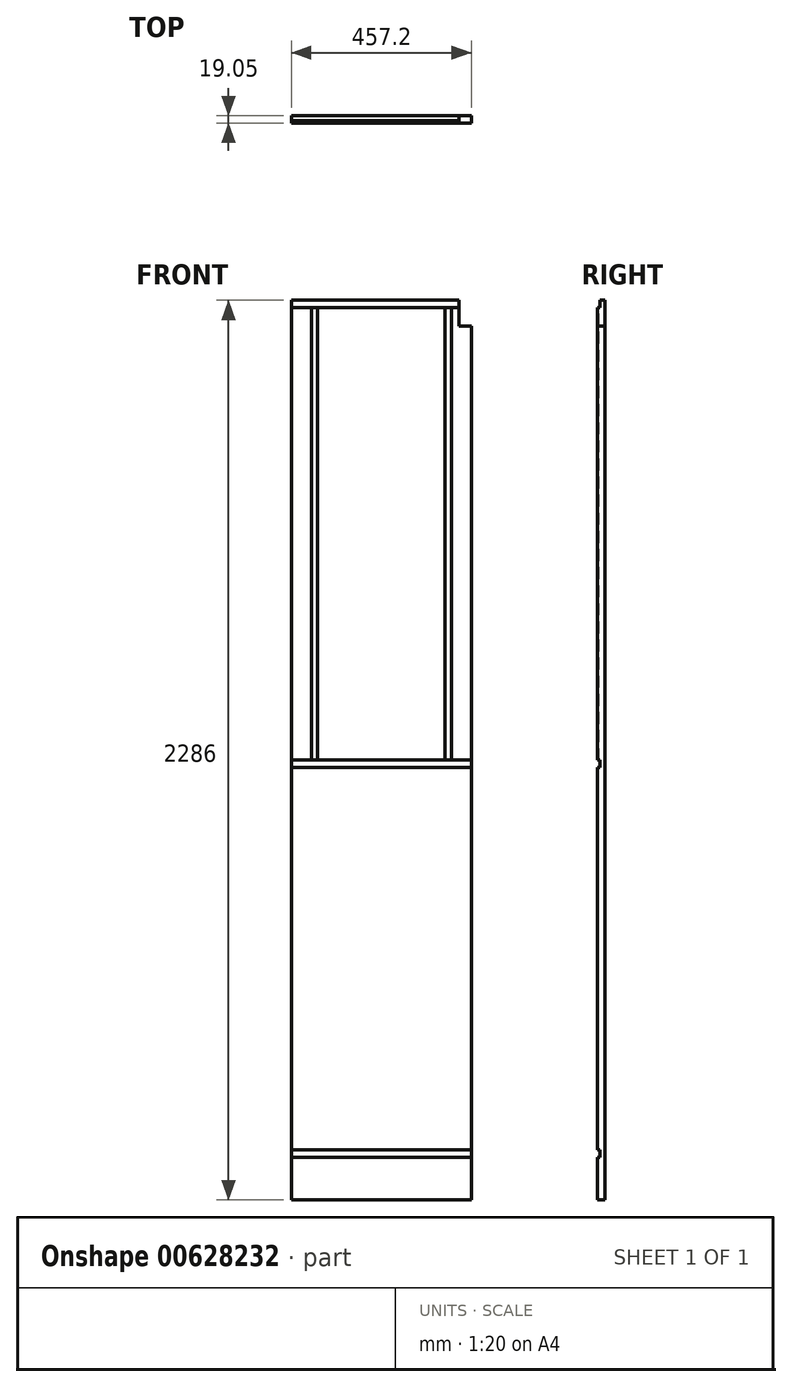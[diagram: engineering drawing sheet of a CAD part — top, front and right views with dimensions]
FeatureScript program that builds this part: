
annotation { "Feature Type Name" : "Feature", "Feature Type Description" : "" }
export const myFeature = defineFeature(function(context is Context, id is Id, definition is map)
    precondition{}
    {
        {
            var Q0;
            Q0=qCreatedBy(makeId("Front.planeOp"),FACE);
            var sketch = newSketch(context, id + "F0", { "sketchPlane" : qUnion([Q0])});
            skLineSegment(sketch, "E0.bottom", {"start": v(0, 0) * mm, "end": v(457.2, 0) * mm});
            skLineSegment(sketch, "E0.top", {"start": v(0, 2286) * mm, "end": v(457.2, 2286) * mm});
            skLineSegment(sketch, "E0.left", {"start": v(0, 0) * mm, "end": v(0, 2286) * mm});
            skLineSegment(sketch, "E0.right", {"start": v(457.2, 0) * mm, "end": v(457.2, 2286) * mm});
            skSolve(sketch);
        }
        {
            var Q0;
            Q0=qSketchRegion(id+"F0",true);
            extrude(context, id + "F1", {"entities" : qUnion([Q0]), "depth" : 19.05 * mm, "offsetDistance" : 25.4 * mm});
        }
        {
            var Q0;
            Q0=makeQuery(id+"F1.opExtrude","CAP_FACE",FACE,{"disambiguationData":[OSD([sQuery(id+"F0.wireOp",EDGE,"E0.bottom"),sQuery(id+"F0.wireOp",EDGE,"E0.top"),sQuery(id+"F0.wireOp",EDGE,"E0.left"),sQuery(id+"F0.wireOp",EDGE,"E0.right")])],"isStart":false});
            var sketch = newSketch(context, id + "F2", { "sketchPlane" : qUnion([Q0])});
            skLineSegment(sketch, "E1.bottom", {"start": v(457.2, 2286) * mm, "end": v(425.2, 2286) * mm});
            skLineSegment(sketch, "E1.top", {"start": v(457.2, 2219.96) * mm, "end": v(425.2, 2219.96) * mm});
            skLineSegment(sketch, "E1.left", {"start": v(457.2, 2286) * mm, "end": v(457.2, 2219.96) * mm});
            skLineSegment(sketch, "E1.right", {"start": v(425.2, 2286) * mm, "end": v(425.2, 2219.96) * mm});
            skSolve(sketch);
        }
        {
            var Q0;
            Q0=makeQuery(id+"F2.imprint","IMPRINT",FACE,{"disambiguationData":[TD([[makeQuery(id+"F2.imprint","IMPRINT",EDGE,{"derivedFrom":sQuery(id+"F2.wireOp",EDGE,"E1.bottom")}),-1.0]])]});
            extrude(context, id + "F3", {"entities" : qUnion([Q0]), "operationType" : NewBodyOperationType.REMOVE, "endBound" : BoundingType.THROUGH_ALL, "oppositeDirection" : true, "depth" : 25.4 * mm, "offsetDistance" : 25.4 * mm});
        }
        {
            var Q0;
            Q0=makeQuery(id+"F1.opExtrude","CAP_FACE",FACE,{"disambiguationData":[OSD([sQuery(id+"F0.wireOp",EDGE,"E0.bottom"),sQuery(id+"F0.wireOp",EDGE,"E0.top"),sQuery(id+"F0.wireOp",EDGE,"E0.left"),sQuery(id+"F0.wireOp",EDGE,"E0.right")])],"isStart":false});
            var sketch = newSketch(context, id + "F4", { "sketchPlane" : qUnion([Q0])});
            skLineSegment(sketch, "E2.bottom", {"start": v(-11.67, 127) * mm, "end": v(519.07, 127) * mm});
            skLineSegment(sketch, "E2.top", {"start": v(-11.67, 107.7) * mm, "end": v(519.07, 107.7) * mm});
            skLineSegment(sketch, "E2.left", {"start": v(-11.67, 127) * mm, "end": v(-11.67, 107.7) * mm});
            skLineSegment(sketch, "E2.right", {"start": v(519.07, 127) * mm, "end": v(519.07, 107.7) * mm});
            skLineSegment(sketch, "E3.bottom", {"start": v(-24.94, 1117.6) * mm, "end": v(528.35, 1117.6) * mm});
            skLineSegment(sketch, "E3.top", {"start": v(-24.94, 1098.3) * mm, "end": v(528.35, 1098.3) * mm});
            skLineSegment(sketch, "E3.left", {"start": v(-24.94, 1117.6) * mm, "end": v(-24.94, 1098.3) * mm});
            skLineSegment(sketch, "E3.right", {"start": v(528.35, 1117.6) * mm, "end": v(528.35, 1098.3) * mm});
            skLineSegment(sketch, "E4.bottom", {"start": v(-16.64, 2295.24) * mm, "end": v(531.9, 2295.24) * mm});
            skLineSegment(sketch, "E4.top", {"start": v(-16.64, 2266.7) * mm, "end": v(531.9, 2266.7) * mm});
            skLineSegment(sketch, "E4.left", {"start": v(-16.64, 2295.24) * mm, "end": v(-16.64, 2266.7) * mm});
            skLineSegment(sketch, "E4.right", {"start": v(531.9, 2295.24) * mm, "end": v(531.9, 2266.7) * mm});
            skSolve(sketch);
        }
        {
            var Q0;
            Q0=qSketchRegion(id+"F4",true);
            extrude(context, id + "F5", {"entities" : qUnion([Q0]), "operationType" : NewBodyOperationType.REMOVE, "oppositeDirection" : true, "depth" : 6.35 * mm, "offsetDistance" : 25.4 * mm});
        }
        {
            var Q0;
            {var subQ0=sQuery(id+"F0.wireOp",EDGE,"E0.left");var subQ1=sQuery(id+"F0.wireOp",EDGE,"E0.right");Q0=makeQuery(id+"F5.boolean.opBoolean","SPLIT",FACE,{"disambiguationData":[TD([makeQuery(id+"F5.opExtrude","SWEPT_FACE",FACE,{"disambiguationData":[OSD([sQuery(id+"F4.wireOp",EDGE,"E3.bottom")])]})])],"derivedFrom":makeQuery(id+"F1.opExtrude","CAP_FACE",FACE,{"disambiguationData":[OSD([sQuery(id+"F0.wireOp",EDGE,"E0.bottom"),sQuery(id+"F0.wireOp",EDGE,"E0.top"),subQ0,subQ1])],"isStart":false})});}
            var sketch = newSketch(context, id + "F6", { "sketchPlane" : qUnion([Q0])});
            skLineSegment(sketch, "E5.bottom", {"start": v(50.8, 1107.77) * mm, "end": v(66.68, 1107.77) * mm});
            skLineSegment(sketch, "E5.top", {"start": v(50.8, 2276.84) * mm, "end": v(66.68, 2276.84) * mm});
            skLineSegment(sketch, "E5.left", {"start": v(50.8, 1107.77) * mm, "end": v(50.8, 2276.84) * mm});
            skLineSegment(sketch, "E5.right", {"start": v(66.68, 1107.77) * mm, "end": v(66.68, 2276.84) * mm});
            skLineSegment(sketch, "E6.bottom", {"start": v(390.52, 1107.5) * mm, "end": v(406.4, 1107.5) * mm});
            skLineSegment(sketch, "E6.top", {"start": v(390.52, 2282.01) * mm, "end": v(406.4, 2282.01) * mm});
            skLineSegment(sketch, "E6.left", {"start": v(390.52, 1107.5) * mm, "end": v(390.52, 2282.01) * mm});
            skLineSegment(sketch, "E6.right", {"start": v(406.4, 1107.5) * mm, "end": v(406.4, 2282.01) * mm});
            skSolve(sketch);
        }
        {
            var Q0;
            Q0=qSketchRegion(id+"F6",true);
            extrude(context, id + "F7", {"entities" : qUnion([Q0]), "operationType" : NewBodyOperationType.REMOVE, "oppositeDirection" : true, "depth" : 4.76 * mm, "offsetDistance" : 25.4 * mm});
        }
    });
